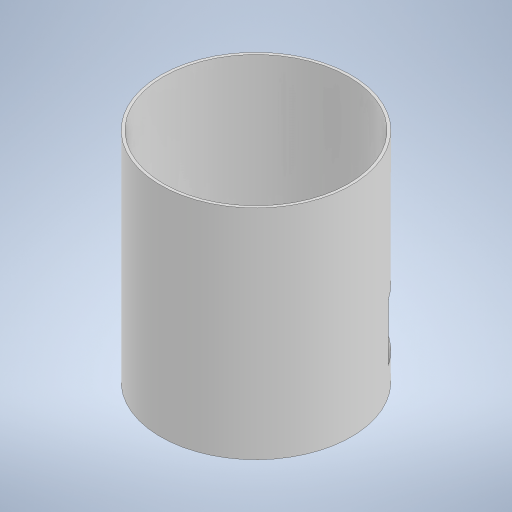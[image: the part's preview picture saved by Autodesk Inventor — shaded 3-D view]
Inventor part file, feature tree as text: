
AUTODESK INVENTOR PART (.ipt)
format: ipt  version: 2024.3 (Build 283343000, 343)  size: 218,624 bytes
history: native  units: mm
features: extrude x2, sketch x2
ambient origin geometry x8: Origin, YZ Plane, XZ Plane, XY Plane, X Axis, Y Axis, Z Axis, Center Point
bodies: Solid1 (feature_tree)
feature tree (4):
  extrude  "Extrusion1"  Depth=140.0mm
  extrude  "Extrusion2"  Depth=42.0mm
  sketch  "Sketch1"  dims[d0=2.0mm d1=140.0mm]
  sketch  "Sketch2"  dims[d2=160.0mm d3=0.0mm d4=42.0mm d5=116.0mm d6=20.0mm d7=58.0mm d8=0.0mm d9=0.0mm]
